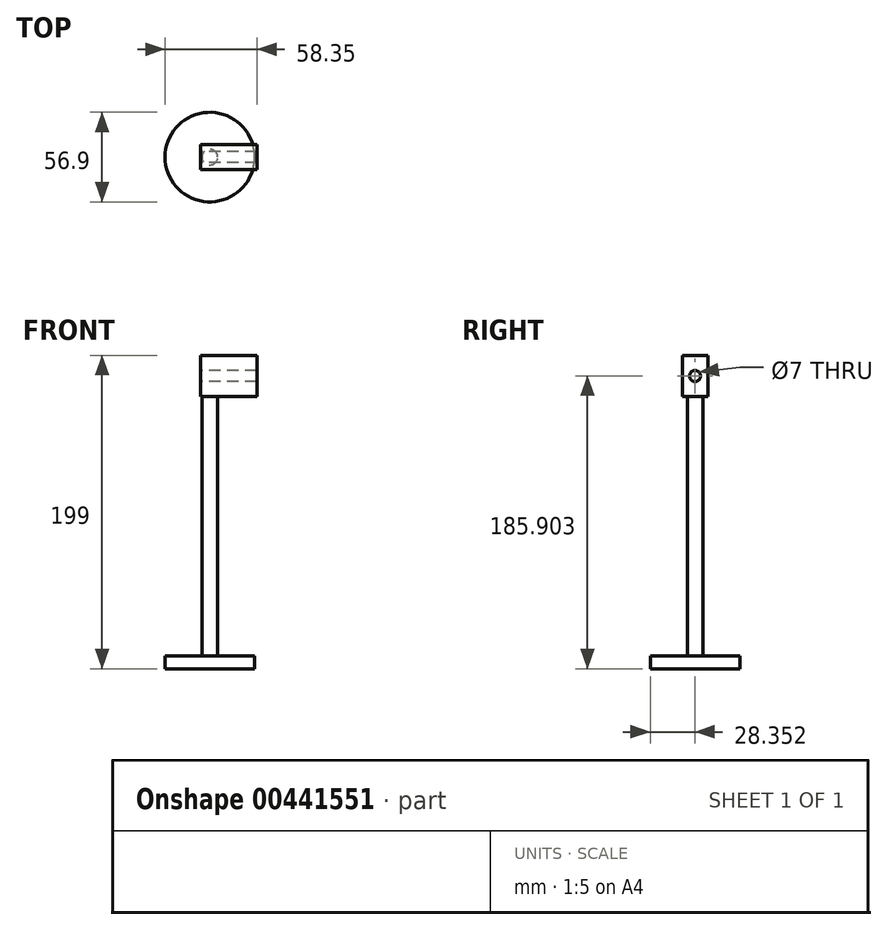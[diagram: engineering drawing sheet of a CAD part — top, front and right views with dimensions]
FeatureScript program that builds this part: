
annotation { "Feature Type Name" : "Feature", "Feature Type Description" : "" }
export const myFeature = defineFeature(function(context is Context, id is Id, definition is map)
    precondition{}
    {
        {
            var Q0;
            Q0=qCreatedBy(makeId("Top.planeOp"),FACE);
            var sketch = newSketch(context, id + "F0", { "sketchPlane" : qUnion([Q0])});
            skCircle(sketch, "E0", {"center": v(0, 0) * mm, "radius": 28.45 * mm});
            skSolve(sketch);
        }
        {
            var Q0;
            Q0 = qSketchRegion(id + "F0", true);
            extrude(context, id + "F1", {"entities" : qUnion([Q0]), "depth" : 8 * mm});
        }
        {
            var Q0;
            Q0=makeQuery(id+"F1.opExtrude","CAP_FACE",FACE,{"disambiguationData":[OSD([sQuery(id+"F0.wireOp",EDGE,"E0")])],"isStart":false});
            var sketch = newSketch(context, id + "F2", { "sketchPlane" : qUnion([Q0])});
            skCircle(sketch, "E1", {"center": v(0, 0) * mm, "radius": 5 * mm});
            skSolve(sketch);
        }
        {
            var Q0;
            Q0 = qSketchRegion(id + "F2", true);
            extrude(context, id + "F3", {"entities" : qUnion([Q0]), "operationType" : NewBodyOperationType.ADD, "depth" : 165 * mm});
        }
        {
            var Q0;
            Q0=qCreatedBy(makeId("Front.planeOp"),FACE);
            var sketch = newSketch(context, id + "F4", { "sketchPlane" : qUnion([Q0])});
            skLineSegment(sketch, "E2.0", {"start": v(-5, 173) * mm, "end": v(5, 173) * mm});
            skLineSegment(sketch, "E3", {"start": v(-6, 173) * mm, "end": v(29.9, 173) * mm});
            skLineSegment(sketch, "E4", {"start": v(29.9, 173) * mm, "end": v(29.9, 199) * mm});
            skLineSegment(sketch, "E5", {"start": v(29.9, 199) * mm, "end": v(-6, 199) * mm});
            skLineSegment(sketch, "E6", {"start": v(-6, 199) * mm, "end": v(-6, 173) * mm});
            skLineSegment(sketch, "E7", {"start": v(-5, 8) * mm, "end": v(-5, 173) * mm});
            skSolve(sketch);
        }
        {
            var Q0;
            Q0 = qSketchRegion(id + "F4", true);
            extrude(context, id + "F5", {"entities" : qUnion([Q0]), "operationType" : NewBodyOperationType.ADD, "endBound" : BoundingType.SYMMETRIC, "depth" : 16 * mm});
        }
        {
            var Q0;
            Q0=makeQuery(id+"F5.opExtrude","SWEPT_FACE",FACE,{"disambiguationData":[OSD([sQuery(id+"F4.wireOp",EDGE,"E6")])]});
            var sketch = newSketch(context, id + "F6", { "sketchPlane" : qUnion([Q0])});
            skCircle(sketch, "E8", {"center": v(0.1, 185.9) * mm, "radius": 3.5 * mm});
            skSolve(sketch);
        }
        {
            var Q0;
            Q0 = qSketchRegion(id + "F6", true);
            extrude(context, id + "F7", {"entities" : qUnion([Q0]), "operationType" : NewBodyOperationType.REMOVE, "oppositeDirection" : true, "depth" : 44 * mm});
        }
    });
